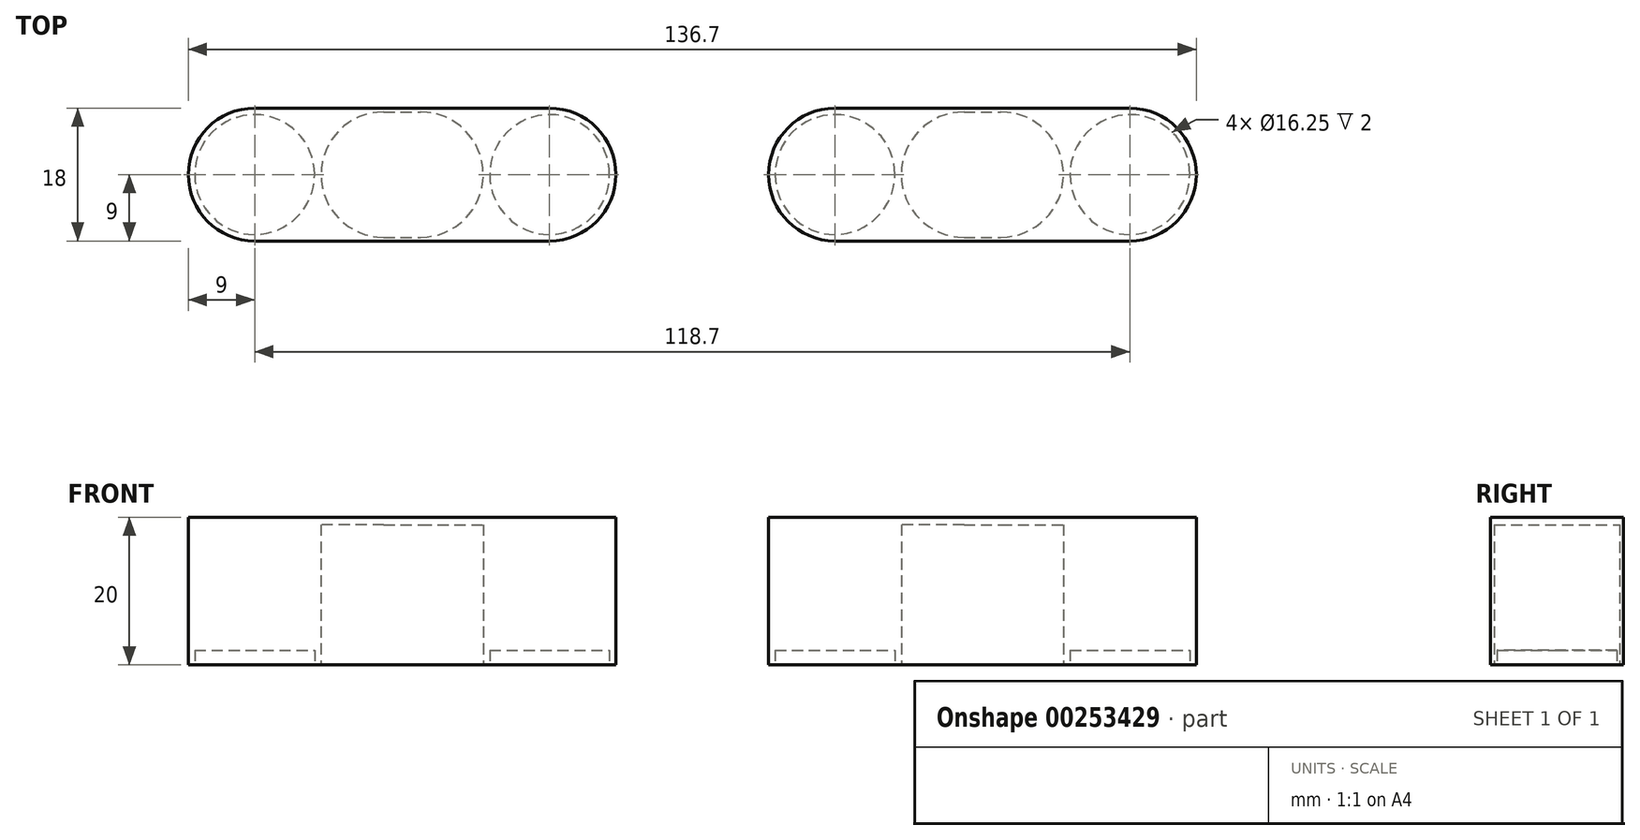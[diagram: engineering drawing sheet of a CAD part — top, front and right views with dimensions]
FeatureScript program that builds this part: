
annotation { "Feature Type Name" : "Feature", "Feature Type Description" : "" }
export const myFeature = defineFeature(function(context is Context, id is Id, definition is map)
    precondition{}
    {
        {
            var Q0;
            Q0=qCreatedBy(makeId("Top.planeOp"),FACE);
            var sketch = newSketch(context, id + "F0", { "sketchPlane" : qUnion([Q0])});
            skLineSegment(sketch, "E0.bottom", {"start": v(20, 9) * mm, "end": v(-20, 9) * mm, "construction": true});
            skLineSegment(sketch, "E0.top", {"start": v(20, -9) * mm, "end": v(-20, -9) * mm, "construction": true});
            skLineSegment(sketch, "E0.left", {"start": v(20, 9) * mm, "end": v(20, -9) * mm, "construction": true});
            skLineSegment(sketch, "E0.right", {"start": v(-20, 9) * mm, "end": v(-20, -9) * mm, "construction": true});
            skPoint(sketch, "E0.middle", {"position": v(0, 0) * mm});
            skArc(sketch, "E1", {"start": v(-20, 9) * mm, "mid": v(-29, 0) * mm, "end": v(-20, -9) * mm});
            skArc(sketch, "E2", {"start": v(20, 9) * mm, "mid": v(29, 0) * mm, "end": v(20, -9) * mm});
            skLineSegment(sketch, "E3", {"start": v(-20, 9) * mm, "end": v(20, 9) * mm});
            skLineSegment(sketch, "E4", {"start": v(-20, -9) * mm, "end": v(20, -9) * mm});
            skSolve(sketch);
        }
        {
            var Q0;
            Q0=makeQuery(id+"F0.imprint","IMPRINT",FACE,{"disambiguationData":[TD([[makeQuery(id+"F0.imprint","IMPRINT",EDGE,{"derivedFrom":sQuery(id+"F0.wireOp",EDGE,"E1")}),1.0]])]});
            extrude(context, id + "F1", {"entities" : qUnion([Q0]), "depth" : 20 * mm});
        }
        {
            var Q0;
            Q0=makeQuery(id+"F1.opExtrude","CAP_FACE",FACE,{"disambiguationData":[OSD([sQuery(id+"F0.wireOp",EDGE,"E1"),sQuery(id+"F0.wireOp",EDGE,"E2"),sQuery(id+"F0.wireOp",EDGE,"E3"),sQuery(id+"F0.wireOp",EDGE,"E4")])],"isStart":true});
            var sketch = newSketch(context, id + "F2", { "sketchPlane" : qUnion([Q0])});
            skCircle(sketch, "E5", {"center": v(-20, 0) * mm, "radius": 8.12 * mm});
            skCircle(sketch, "E6", {"center": v(20, 0) * mm, "radius": 8.12 * mm});
            skLineSegment(sketch, "E7.bottom", {"start": v(2.5, 8.5) * mm, "end": v(-2.5, 8.5) * mm, "construction": true});
            skLineSegment(sketch, "E7.top", {"start": v(2.5, -8.5) * mm, "end": v(-2.5, -8.5) * mm, "construction": true});
            skLineSegment(sketch, "E7.left", {"start": v(2.5, 8.5) * mm, "end": v(2.5, -8.5) * mm, "construction": true});
            skLineSegment(sketch, "E7.right", {"start": v(-2.5, 8.5) * mm, "end": v(-2.5, -8.5) * mm, "construction": true});
            skPoint(sketch, "E7.middle", {"position": v(0, 0) * mm});
            skArc(sketch, "E8", {"start": v(-2.5, 8.5) * mm, "mid": v(-11, 0) * mm, "end": v(-2.5, -8.5) * mm});
            skArc(sketch, "E9", {"start": v(2.5, 8.5) * mm, "mid": v(11, 0) * mm, "end": v(2.5, -8.5) * mm});
            skLineSegment(sketch, "E10", {"start": v(-2.5, 8.5) * mm, "end": v(2.5, 8.5) * mm});
            skLineSegment(sketch, "E11", {"start": v(-2.5, -8.5) * mm, "end": v(2.5, -8.5) * mm});
            skSolve(sketch);
        }
        {
            var Q0;
            Q0=makeQuery(id+"F2.imprint","IMPRINT",FACE,{"disambiguationData":[TD([[makeQuery(id+"F2.imprint","IMPRINT",EDGE,{"derivedFrom":sQuery(id+"F2.wireOp",EDGE,"E5")}),1.0]])]});
            var Q1;
            Q1=makeQuery(id+"F2.imprint","IMPRINT",FACE,{"disambiguationData":[TD([[makeQuery(id+"F2.imprint","IMPRINT",EDGE,{"derivedFrom":sQuery(id+"F2.wireOp",EDGE,"E6")}),1.0]])]});
            extrude(context, id + "F3", {"entities" : qUnion([Q0, Q1]), "operationType" : NewBodyOperationType.REMOVE, "oppositeDirection" : true, "depth" : 2 * mm});
        }
        {
            var Q0;
            Q0=makeQuery(id+"F2.imprint","IMPRINT",FACE,{"disambiguationData":[TD([[makeQuery(id+"F2.imprint","IMPRINT",EDGE,{"derivedFrom":sQuery(id+"F2.wireOp",EDGE,"cOhPUrrm-RYIU-x7wC-9qj7-ESWvJqnapW1Z")}),1.0]])]});
            var Q1;
            Q1=makeQuery(id+"F2.imprint","IMPRINT",FACE,{"disambiguationData":[TD([[makeQuery(id+"F2.imprint","IMPRINT",EDGE,{"derivedFrom":sQuery(id+"F2.wireOp",EDGE,"E8")}),1.0]])]});
            extrude(context, id + "F4", {"entities" : qUnion([Q0, Q1]), "operationType" : NewBodyOperationType.REMOVE, "oppositeDirection" : true, "depth" : 19 * mm});
        }
        {
            var Q0;
            Q0=makeQuery(id+"F1.opExtrude","SWEPT_BODY",BODY,{"disambiguationData":[OSD([sQuery(id+"F0.wireOp",EDGE,"E1"),sQuery(id+"F0.wireOp",EDGE,"E2"),sQuery(id+"F0.wireOp",EDGE,"E3"),sQuery(id+"F0.wireOp",EDGE,"E4")])]});
            transform(context, id + "F5", {"entities" : qUnion([Q0]), "transformType" : TransformType.TRANSLATION_3D, "dx" : 78.7 * mm, "dy" : 0 * mm, "dz" : 0 * mm, "makeCopy" : true});
        }
    });
